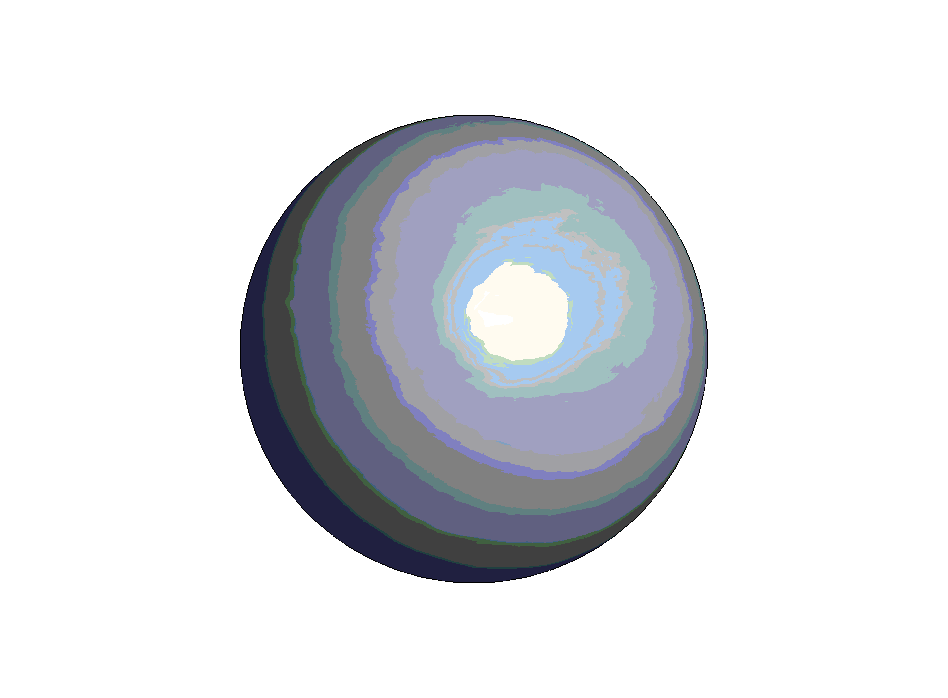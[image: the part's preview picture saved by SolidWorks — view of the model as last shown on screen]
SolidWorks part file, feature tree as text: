
SOLIDWORKS PART (.sldprt)
format: sldprt  version: not decoded by parser v0  size: 1,462,272 bytes
history: native  units: mm
features: sketch x8, cut_revolve x4, plane x3, cut_extrude x3, material x1, revolve x1, thread x1, chamfer x1 + 3 further entries (+9 scaffold rows collapsed)
feature tree (34):
  scaffold x9  (default folders/planes/origin — collapsed)
  material  "Stainless Steel 440C 58Rc"
  plane  "Plane X-Y"
  plane  "Plane X-Z"
  plane  "Plane Y-Z"
  "Design Table"
  "Axis - Y"
  "Axis - Z"
  sketch  "Sketch1"  dims[Ball_Diameter=12.7mm D2=25.4mm]
  revolve  "Complete_Ball"  Angle=360deg
  sketch  "Sketch2"  dims[D1=~11.961647mm D2=8.4836mm]
  cut_extrude  "Truncated_ball"  [1 undecoded]
  sketch  "Sketch3"  dims[D1=8.255mm]
  cut_extrude  "Recessed"  Depth=0.127mm
  sketch  "Sketch4"  dims[D1=4.953mm]
  cut_extrude  "Threaded"  [1 undecoded]
  thread  "Cosmetic Thread1"  Diameter=6.35mm  [1 undecoded]
  chamfer  "Chamfer1"  Distance=0.254mm Angle=45deg
  sketch  "Sketch5"  dims[c1.D1=7.1374mm c1.D2=3.9116mm c2.D1=3.5052mm c2.D3=7.1374mm]
  cut_revolve  "Counterbored_hole"  Angle=360deg
  sketch  "Sketch6"  dims[D1=3.9116mm D2=7.1374mm D3=3.5052mm]
  cut_revolve  "Full_ball_CtBored_hole"  Angle=360deg
  sketch  "Sketch7"  dims[D1=3.175mm D2=6.35mm]
  cut_revolve  "Ball_w_concentric_hole"  Angle=360deg
  sketch  "Sketch8"  dims[D1=4.7625mm D2=3.175mm]
  cut_revolve  "Truncated_ball_w_blind_hole"  Angle=360deg
decode coverage: 16 of 18 modeling features carry decoded parameters; 3 rows unclassified (native names shown)
note: ~ marks probable driven/reference dimensions
note: 3 parameter values undecoded
note: suppression state not decoded; provenance and decode notes live in map.json
